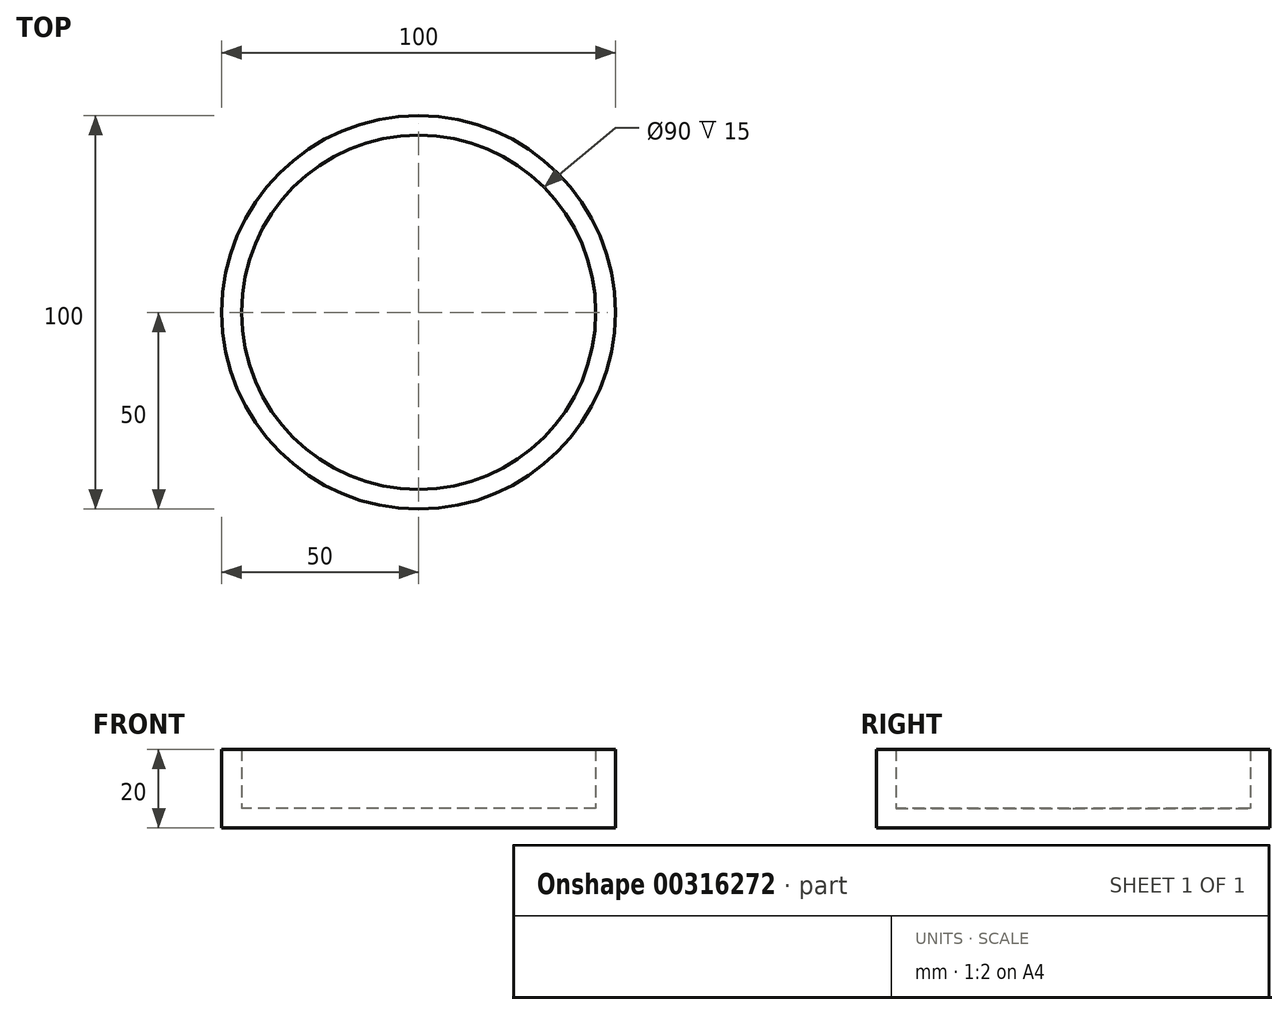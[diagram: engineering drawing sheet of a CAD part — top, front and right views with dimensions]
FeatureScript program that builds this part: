
annotation { "Feature Type Name" : "Feature", "Feature Type Description" : "" }
export const myFeature = defineFeature(function(context is Context, id is Id, definition is map)
    precondition{}
    {
        {
            var Q0;
            Q0=qCreatedBy(makeId("Top.planeOp"),FACE);
            var sketch = newSketch(context, id + "F0", { "sketchPlane" : qUnion([Q0])});
            skCircle(sketch, "E0", {"center": v(0, 0) * mm, "radius": 45 * mm});
            skCircle(sketch, "E1", {"center": v(0, 0) * mm, "radius": 50 * mm});
            skSolve(sketch);
        }
        {
            var Q0;
            Q0=makeQuery(id+"F0.imprint","IMPRINT",FACE,{"disambiguationData":[TD([[makeQuery(id+"F0.imprint","IMPRINT",EDGE,{"derivedFrom":sQuery(id+"F0.wireOp",EDGE,"E0")}),1.0]])]});
            extrude(context, id + "F1", {"entities" : qUnion([Q0]), "depth" : 5 * mm});
        }
        {
            var Q0;
            Q0 = qSketchRegion(id + "F0", true);
            extrude(context, id + "F2", {"entities" : qUnion([Q0]), "operationType" : NewBodyOperationType.ADD, "depth" : 20 * mm});
        }
        {
            var Q0;
            Q0=makeQuery(id+"F2.opExtrude","CAP_EDGE",EDGE,{"disambiguationData":[OSD([sQuery(id+"F0.wireOp",EDGE,"E1")])],"isStart":true});
            chamfer(context, id + "F3", {"entities" : qUnion([Q0]), "chamferType" : ChamferType.TWO_OFFSETS, "width1" : 5 * mm, "oppositeDirection" : false, "width2" : 5 * mm, "tangentPropagation" : true});
        }
        {
            var Q0;
            Q0=makeQuery(id+"F2.opExtrude","CAP_EDGE",EDGE,{"disambiguationData":[OSD([sQuery(id+"F0.wireOp",EDGE,"E0")])],"isStart":false});
            chamfer(context, id + "F4", {"entities" : qUnion([Q0]), "chamferType" : ChamferType.TWO_OFFSETS, "width1" : 10 * mm, "oppositeDirection" : false, "width2" : 5 * mm, "tangentPropagation" : true});
        }
        {
            var Q0;
            Q0 = qSketchRegion(id + "F0", true);
            extrude(context, id + "F5", {"entities" : qUnion([Q0]), "operationType" : NewBodyOperationType.ADD, "depth" : 20 * mm});
        }
    });
